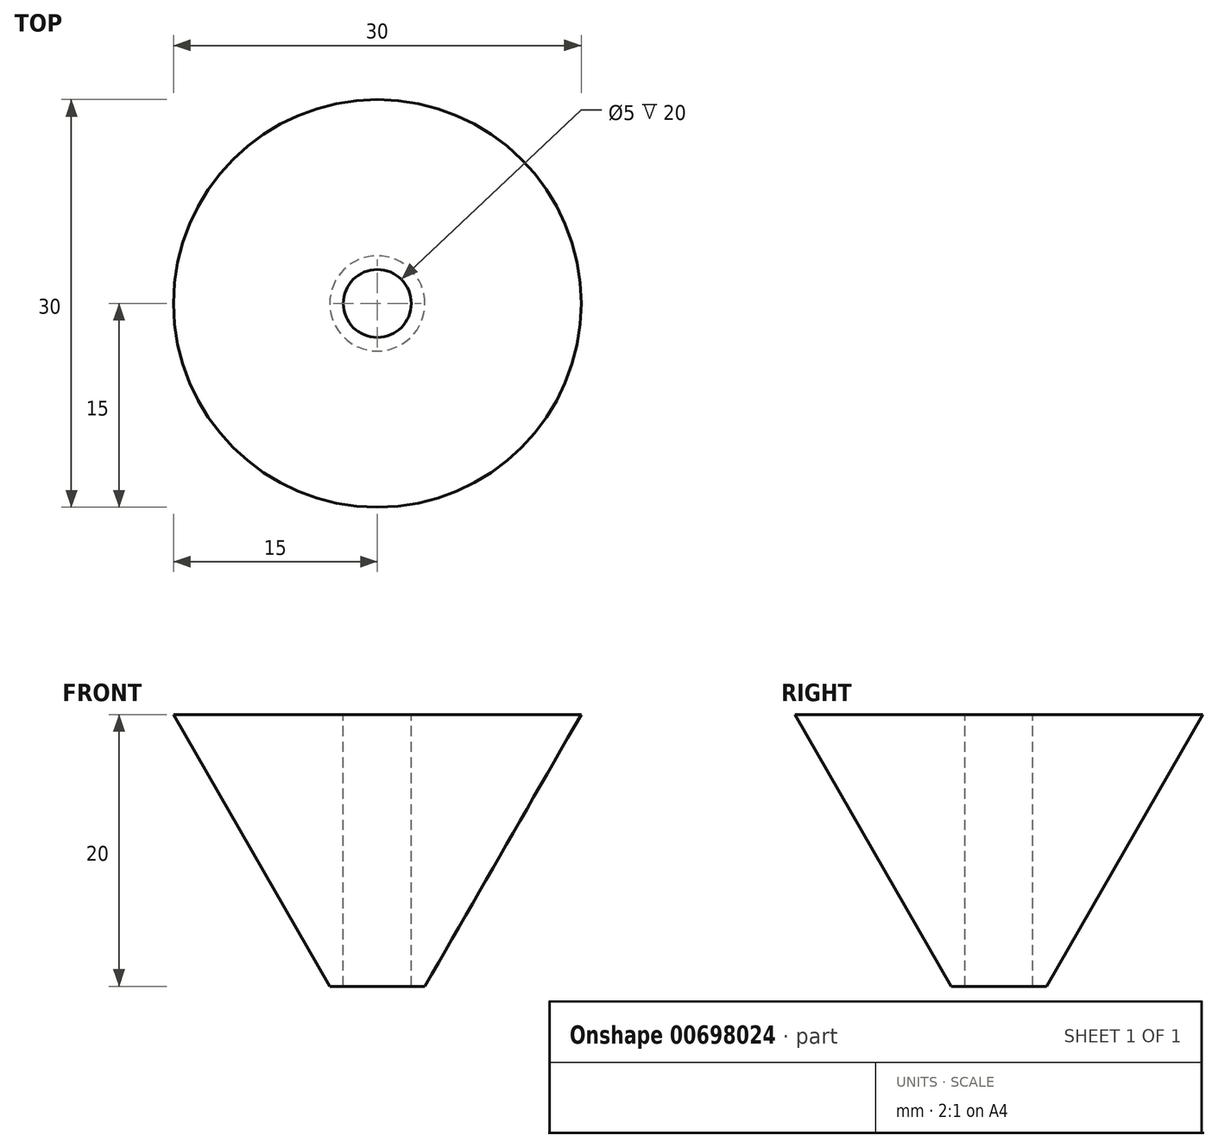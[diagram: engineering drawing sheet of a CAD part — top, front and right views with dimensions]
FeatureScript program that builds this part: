
annotation { "Feature Type Name" : "Feature", "Feature Type Description" : "" }
export const myFeature = defineFeature(function(context is Context, id is Id, definition is map)
    precondition{}
    {
        {
            var Q0;
            Q0=qCreatedBy(makeId("Front.planeOp"),FACE);
            var sketch = newSketch(context, id + "F0", { "sketchPlane" : qUnion([Q0])});
            skLineSegment(sketch, "E0", {"start": v(0, 30) * mm, "end": v(0, 0) * mm});
            skLineSegment(sketch, "E1", {"start": v(2.5, 0) * mm, "end": v(2.5, 20) * mm});
            skLineSegment(sketch, "E2", {"start": v(2.5, 20) * mm, "end": v(15, 20) * mm});
            skLineSegment(sketch, "E3", {"start": v(15, 20) * mm, "end": v(3.5, 0) * mm});
            skLineSegment(sketch, "E4", {"start": v(3.5, 0) * mm, "end": v(2.5, 0) * mm});
            skSolve(sketch);
        }
        {
            var Q0;
            Q0=qSketchRegion(id+"F0",true);
            var Q1;
            Q1=sQuery(id+"F0.wireOp",EDGE,"E0");
            revolve(context, id + "F1", {"entities" : qUnion([Q0]), "axis" : qUnion([Q1]), "revolveType" : RevolveType.FULL});
        }
    });
